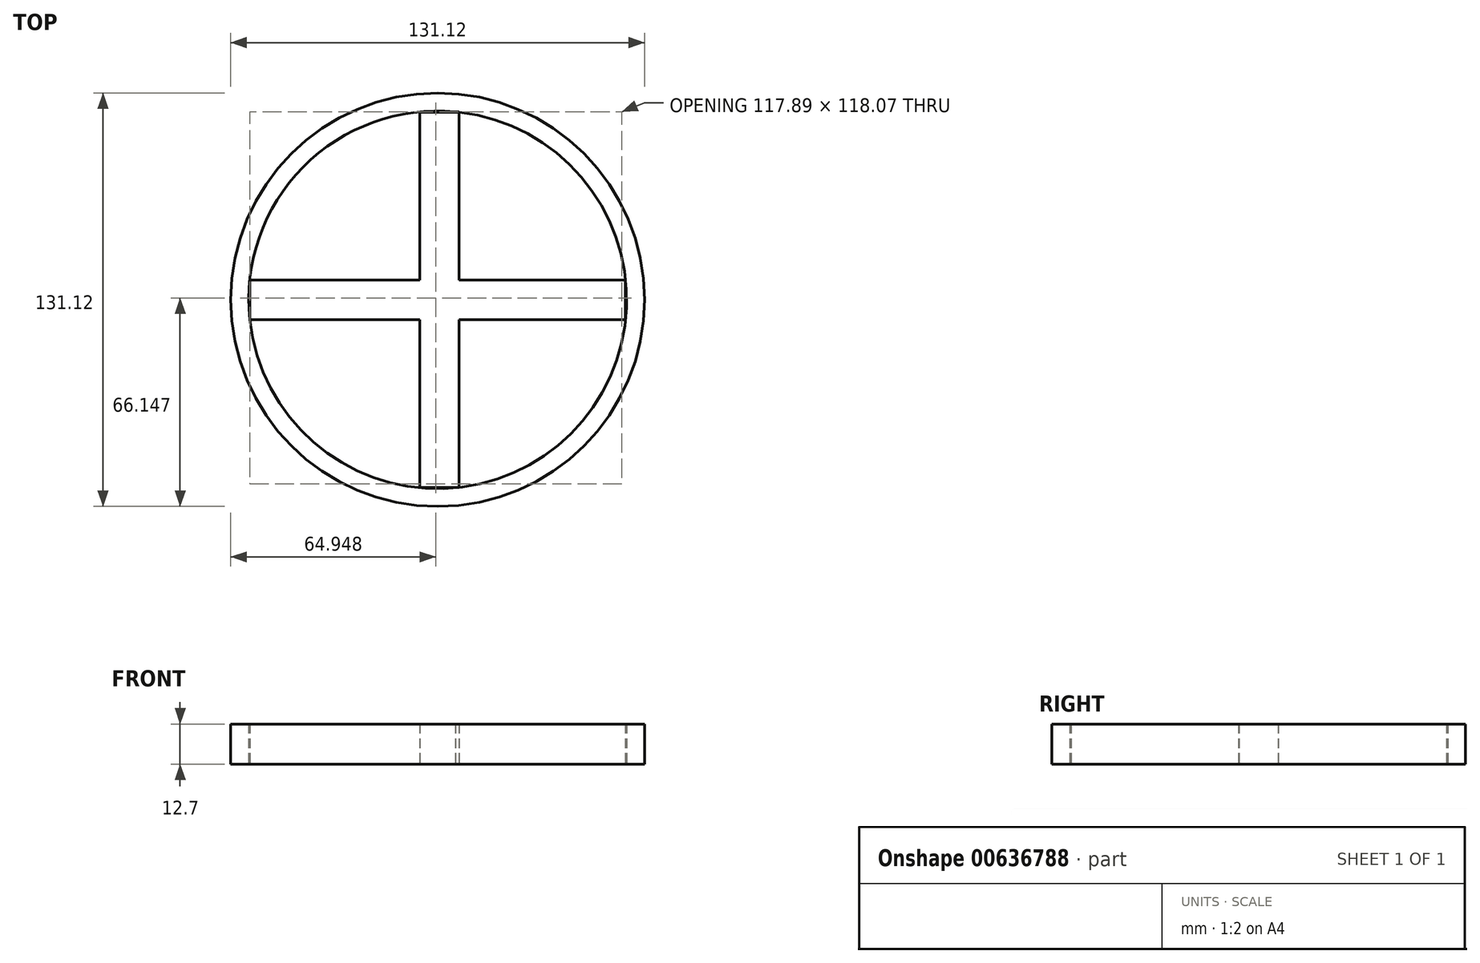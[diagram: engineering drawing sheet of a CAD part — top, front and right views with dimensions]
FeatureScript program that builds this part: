
annotation { "Feature Type Name" : "Feature", "Feature Type Description" : "" }
export const myFeature = defineFeature(function(context is Context, id is Id, definition is map)
    precondition{}
    {
        {
            var Q0;
            Q0=qCreatedBy(makeId("Top.planeOp"),FACE);
            var sketch = newSketch(context, id + "F0", { "sketchPlane" : qUnion([Q0])});
            skCircle(sketch, "E0", {"center": v(0, 0) * mm, "radius": 65.56 * mm});
            skCircle(sketch, "E1", {"center": v(0, 0) * mm, "radius": 59.89 * mm});
            skLineSegment(sketch, "E2.bottom", {"start": v(-5.62, 59.62) * mm, "end": v(6.83, 59.62) * mm});
            skLineSegment(sketch, "E2.top", {"start": v(-5.62, 59.5) * mm, "end": v(6.83, 59.5) * mm});
            skLineSegment(sketch, "E2.left", {"start": v(-5.62, 59.62) * mm, "end": v(-5.62, 59.5) * mm});
            skLineSegment(sketch, "E2.right", {"start": v(6.83, 59.62) * mm, "end": v(6.83, 59.5) * mm});
            skLineSegment(sketch, "E3.top", {"start": v(-5.62, -59.5) * mm, "end": v(6.83, -59.5) * mm});
            skLineSegment(sketch, "E3.left", {"start": v(-5.62, 59.62) * mm, "end": v(-5.62, -59.5) * mm});
            skLineSegment(sketch, "E3.right", {"start": v(6.83, 59.62) * mm, "end": v(6.83, -59.5) * mm});
            skLineSegment(sketch, "E4.bottom", {"start": v(-59.56, 6.26) * mm, "end": v(59.55, 6.26) * mm});
            skLineSegment(sketch, "E4.top", {"start": v(-59.56, -6.32) * mm, "end": v(59.55, -6.32) * mm});
            skLineSegment(sketch, "E4.left", {"start": v(-59.56, 6.26) * mm, "end": v(-59.56, -6.32) * mm});
            skLineSegment(sketch, "E4.right", {"start": v(59.55, 6.26) * mm, "end": v(59.55, -6.32) * mm});
            skSolve(sketch);
        }
        {
            var Q0;
            Q0=makeQuery(id+"F0.imprint","IMPRINT",FACE,{"disambiguationData":[TD([[makeQuery(id+"F0.imprint","IMPRINT",EDGE,{"derivedFrom":sQuery(id+"F0.wireOp",EDGE,"E0")}),1.0]])]});
            var Q1;
            {var subQ0=sQuery(id+"F0.wireOp",EDGE,"E4.left");var subQ2=sQuery(id+"F0.wireOp",EDGE,"E1");var subQ9=makeQuery(id+"F0.imprint","INTERSECT",VERTEX,{"derivedFrom":[subQ2,subQ0]});Q1=makeQuery(id+"F0.imprint","IMPRINT",FACE,{"disambiguationData":[TD([[makeQuery(id+"F0.imprint","IMPRINT",EDGE,{"disambiguationData":[TD([[subQ9,-1.0]])],"derivedFrom":subQ2}),1.0]])]});}
            var Q2;
            {var subQ0=sQuery(id+"F0.wireOp",EDGE,"E3.top");Q2=makeQuery(id+"F0.imprint","IMPRINT",FACE,{"disambiguationData":[TD([[makeQuery(id+"F0.imprint","IMPRINT",EDGE,{"derivedFrom":subQ0}),1.0]])]});}
            var Q3;
            {var subQ0=sQuery(id+"F0.wireOp",EDGE,"E4.bottom");var subQ1=sQuery(id+"F0.wireOp",EDGE,"E3.left");var subQ2=makeQuery(id+"F0.imprint","INTERSECT",VERTEX,{"derivedFrom":[subQ1,subQ0]});Q3=makeQuery(id+"F0.imprint","IMPRINT",FACE,{"disambiguationData":[TD([[makeQuery(id+"F0.imprint","IMPRINT",EDGE,{"disambiguationData":[TD([[subQ2,-1.0]])],"derivedFrom":subQ1}),1.0]])]});}
            var Q4;
            {var subQ5=sQuery(id+"F0.wireOp",EDGE,"E4.right");Q4=makeQuery(id+"F0.imprint","IMPRINT",FACE,{"disambiguationData":[TD([[makeQuery(id+"F0.imprint","IMPRINT",EDGE,{"derivedFrom":subQ5}),-1.0]])]});}
            var Q5;
            {var subQ0=sQuery(id+"F0.wireOp",EDGE,"E2.top");Q5=makeQuery(id+"F0.imprint","IMPRINT",FACE,{"disambiguationData":[TD([[makeQuery(id+"F0.imprint","IMPRINT",EDGE,{"derivedFrom":subQ0}),-1.0]])]});}
            extrude(context, id + "F1", {"entities" : qUnion([Q0, Q1, Q2, Q3, Q4, Q5]), "depth" : 12.7 * mm, "offsetDistance" : 25.4 * mm});
        }
    });
